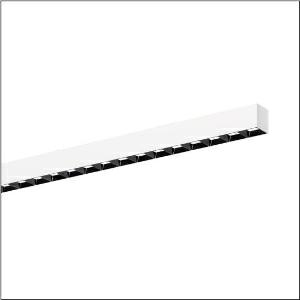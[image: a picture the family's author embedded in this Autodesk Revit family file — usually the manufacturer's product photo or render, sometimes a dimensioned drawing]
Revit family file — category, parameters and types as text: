
# Revit family: silica_r__21_51mx21dc3awb_ae09
name_source: partatom
category: Lighting Fixtures
units: mm (PartAtom-declared; Revit-internal decimal feet)

## family parameters
Cut with Voids When Loaded = No
Host = Face
Light Source = No
Part Type = Normal
Room Calculation Point = No
Round Connector Dimension = Use Diameter
Shared = No

## types (1)
- --- (1 x LED, 10800 lm, 69.3 W, 3000K)
    Apparent Load = 69 VA
    CIE Flux Codes = 87 99 100 100 100
    Color Rendering = 80
    Color Temperature = 3000K
    Default Elevation = 1800 mm
    Description = Silica® 21, office luminaire, primary light control with darklight reflector, of PMMA, black, CAT 2 (L<= 3000cd/m²), light emission: direct distribution, primary light characteristic: symmetric, installation type: surface-mounted, LED, rated luminous flux: 10.800lm, luminous efficacy: 156lm/W, light colour: 830, colour temperature: 3000K, with terminal, 3+2-pole, max. 2.5mm², mains connection: 220..240V, AC, 50/60Hz, luminaire housing, of aluminium, traffic white (RAL 9016), length: 3.004mm, width: 53mm, height: 53mm, protection rating (complete): IP20, insulation class (complete): insulation class I (protective earthing), certification: CE, permissible operating ambient temperature: 0..+35°C, standard: EN 50419, packaging unit: 1 piece
    Height = 0 mm  [stored 0 ft]
    Lamp = 1 x LED
    Lamp Light Flux = 10800 lm
    Lamp Power = 69.3 W
    Lamp count = 1
    Length = 3004 mm
    Luminous efficacy = 156 lm/W
    Manufacturer = Siteco
    ModVariant = No
    Model = 51MX21DC3AWB
    Mounting Place = Ceiling
    Mounting Type = Recessed
    Number of Poles = 1
    OnlyDefault = Yes
    Power Factor = 1
    Product Name = Silica® 21
    Product group = office luminaire | ceiling recessed
    ProductGroupID = 400
    Protection Class = Protection class I
    Protection Degree = IP 20
    RLX_Detail_Level = 1
    RLX_Emergency_Light_Flux = 0 lm
    RLX_Emergency_Type = 0
    RLX_Emergency_Type_DB = No
    RlxData = <blob elided: 61521 chars, md5=f8fdfb57>
    Socket = socket
    Standby Power = 0 W
    System Light Flux = 10800 lm
    System Power = 69 W
    Type Comments = factory setting: luminous flux: 100 % | dim-lin: 254 | 393 mA
    Type Image = l_1335873.jpg
    URL = http://relux.com
    VarID = @adj_093587
    Voltage = 0 V
    Weight = 0.00 kg
    Width = 53 mm

note: [stored X ft] marks values corroborated as IEEE doubles in the binary element streams (Revit-internal decimal feet)

## geometry (parser evidence)
native form markers: Blend x4, Sweep x12
no freeform markers — native parametric forms only
